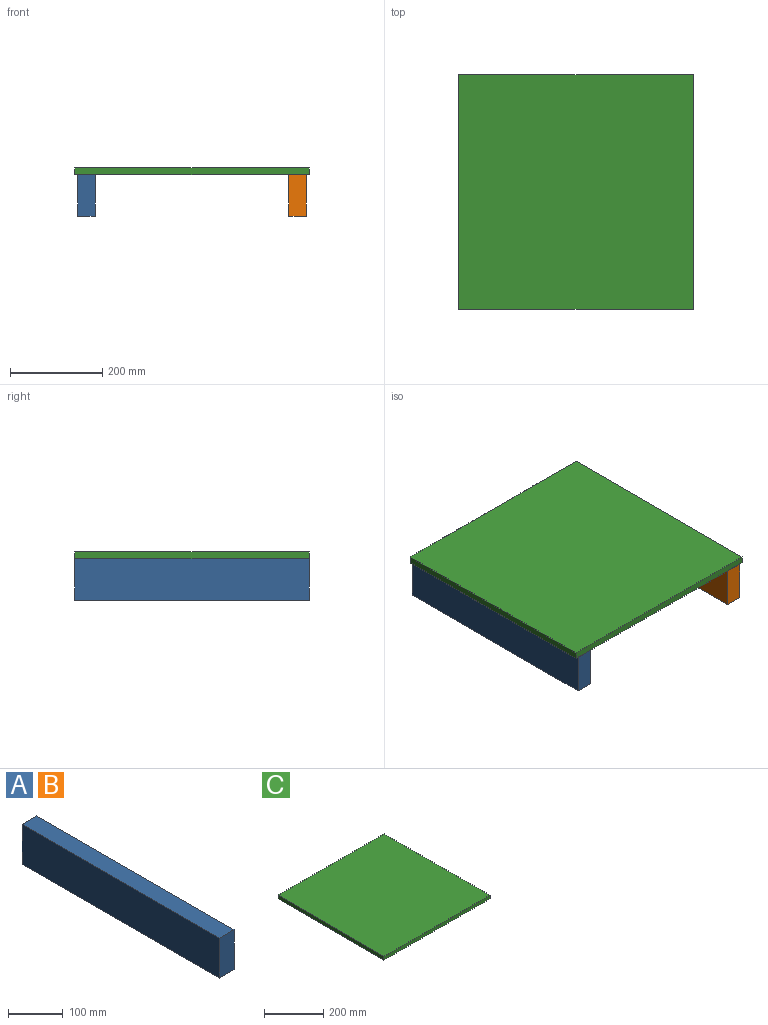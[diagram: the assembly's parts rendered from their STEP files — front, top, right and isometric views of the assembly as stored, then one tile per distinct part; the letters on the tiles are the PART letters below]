
ASSEMBLY  parts=3 mates=1
PART A: 6 faces, bbox 38.1x508x88.9 mm
  f0: plane 508x88.9mm, normal (-1,0,0), area 45161.2mm2, adj f1,f3,f4,f5
  f1: plane 508x38.1mm, normal (0,0,-1), area 19354.8mm2, adj f0,f2,f4,f5
  f2: plane 508x88.9mm, normal (1,0,0), area 45161.2mm2, adj f1,f3,f4,f5
  f3: plane 508x38.1mm, normal (0,0,1), area 19354.8mm2, adj f0,f2,f4,f5
  f4: plane 88.9x38.1mm, normal (0,-1,0), area 3387.1mm2, adj f0,f1,f2,f3
  f5: plane 88.9x38.1mm, normal (0,1,0), area 3387.1mm2, adj f0,f1,f2,f3
PART B: same geometry as A
PART C: 6 faces, bbox 508x508x15.1 mm
  f0: plane 508x15.08mm, normal (0,1,0), area 7661.3mm2, adj f1,f3,f4,f5
  f1: plane 508x15.08mm, normal (-1,0,0), area 7661.3mm2, adj f0,f2,f4,f5
  f2: plane 508x15.08mm, normal (0,-1,0), area 7661.3mm2, adj f1,f3,f4,f5
  f3: plane 508x15.08mm, normal (1,0,0), area 7661.3mm2, adj f0,f2,f4,f5
  f4: plane 508x508mm, normal (0,0,1), area 258064mm2, adj f0,f1,f2,f3
  f5: plane 508x508mm, normal (0,0,-1), area 258064mm2, adj f0,f1,f2,f3
PLACE A t=(-247.65,254,-103.98)mm
PLACE B t=(209.55,254,-103.98)mm
PLACE C t=(-254,254,-15.08)mm
MATE fastened B.f3 <-> C.f5  axis (0,0,1) through (247.65,-254,-15.08)mm
